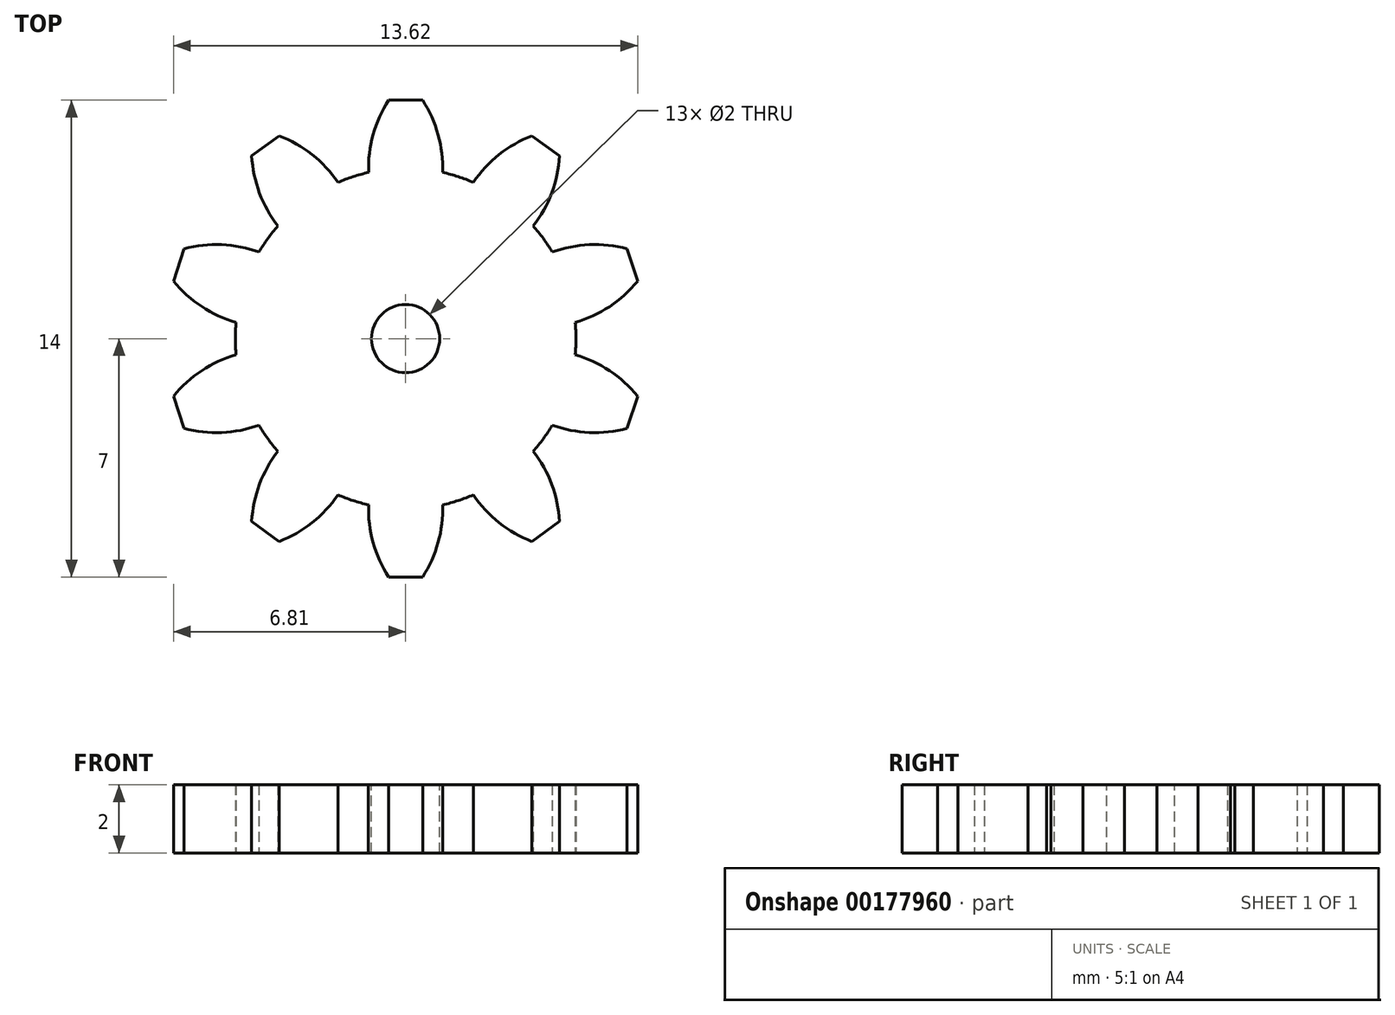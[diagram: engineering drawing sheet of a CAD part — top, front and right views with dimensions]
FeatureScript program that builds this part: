
annotation { "Feature Type Name" : "Feature", "Feature Type Description" : "" }
export const myFeature = defineFeature(function(context is Context, id is Id, definition is map)
    precondition{}
    {
        {
            var Q0;
            Q0=qCreatedBy(makeId("Top.planeOp"),FACE);
            var sketch = newSketch(context, id + "F0", { "sketchPlane" : qUnion([Q0])});
            skCircle(sketch, "E0", {"center": v(0, 0) * mm, "radius": 5 * mm});
            skLineSegment(sketch, "E1", {"start": v(0, 0) * mm, "end": v(0, 5) * mm, "construction": true});
            skLineSegment(sketch, "E2", {"start": v(0, 7) * mm, "end": v(-0.5, 7) * mm});
            skArc(sketch, "E3", {"start": v(-0.5, 7) * mm, "mid": v(-0.96, 5.98) * mm, "end": v(-1.09, 4.88) * mm});
            skArc(sketch, "E4.MirrorCS", {"start": v(0.5, 7) * mm, "mid": v(0.96, 5.98) * mm, "end": v(1.09, 4.88) * mm});
            skLineSegment(sketch, "E5.MirrorCS", {"start": v(0, 7) * mm, "end": v(0.5, 7) * mm});
            skArc(sketch, "E6.1.0", {"start": v(-4.52, 5.37) * mm, "mid": v(-4.3, 4.28) * mm, "end": v(-3.75, 3.3) * mm});
            skLineSegment(sketch, "E6.1.1", {"start": v(-4.11, 5.66) * mm, "end": v(-4.52, 5.37) * mm});
            skLineSegment(sketch, "E6.1.2", {"start": v(-4.11, 5.66) * mm, "end": v(-3.7, 5.96) * mm});
            skArc(sketch, "E6.1.3", {"start": v(-3.7, 5.96) * mm, "mid": v(-2.75, 5.4) * mm, "end": v(-1.99, 4.59) * mm});
            skArc(sketch, "E6.2.0", {"start": v(-6.81, 1.69) * mm, "mid": v(-5.99, 0.94) * mm, "end": v(-4.98, 0.47) * mm});
            skLineSegment(sketch, "E6.2.1", {"start": v(-6.66, 2.16) * mm, "end": v(-6.81, 1.69) * mm});
            skLineSegment(sketch, "E6.2.2", {"start": v(-6.66, 2.16) * mm, "end": v(-6.5, 2.64) * mm});
            skArc(sketch, "E6.2.3", {"start": v(-6.5, 2.64) * mm, "mid": v(-5.4, 2.76) * mm, "end": v(-4.3, 2.54) * mm});
            skArc(sketch, "E6.3.0", {"start": v(-6.5, -2.64) * mm, "mid": v(-5.4, -2.76) * mm, "end": v(-4.3, -2.54) * mm});
            skLineSegment(sketch, "E6.3.1", {"start": v(-6.66, -2.16) * mm, "end": v(-6.5, -2.64) * mm});
            skLineSegment(sketch, "E6.3.2", {"start": v(-6.66, -2.16) * mm, "end": v(-6.81, -1.69) * mm});
            skArc(sketch, "E6.3.3", {"start": v(-6.81, -1.69) * mm, "mid": v(-5.99, -0.94) * mm, "end": v(-4.98, -0.47) * mm});
            skArc(sketch, "E6.4.0", {"start": v(-3.7, -5.96) * mm, "mid": v(-2.75, -5.4) * mm, "end": v(-1.99, -4.59) * mm});
            skLineSegment(sketch, "E6.4.1", {"start": v(-4.11, -5.66) * mm, "end": v(-3.7, -5.96) * mm});
            skLineSegment(sketch, "E6.4.2", {"start": v(-4.11, -5.66) * mm, "end": v(-4.52, -5.37) * mm});
            skArc(sketch, "E6.4.3", {"start": v(-4.52, -5.37) * mm, "mid": v(-4.3, -4.28) * mm, "end": v(-3.75, -3.3) * mm});
            skArc(sketch, "E6.5.0", {"start": v(0.5, -7) * mm, "mid": v(0.96, -5.98) * mm, "end": v(1.09, -4.88) * mm});
            skLineSegment(sketch, "E6.5.1", {"start": v(0, -7) * mm, "end": v(0.5, -7) * mm});
            skLineSegment(sketch, "E6.5.2", {"start": v(0, -7) * mm, "end": v(-0.5, -7) * mm});
            skArc(sketch, "E6.5.3", {"start": v(-0.5, -7) * mm, "mid": v(-0.96, -5.98) * mm, "end": v(-1.09, -4.88) * mm});
            skArc(sketch, "E6.6.0", {"start": v(4.52, -5.37) * mm, "mid": v(4.3, -4.28) * mm, "end": v(3.75, -3.3) * mm});
            skLineSegment(sketch, "E6.6.1", {"start": v(4.11, -5.66) * mm, "end": v(4.52, -5.37) * mm});
            skLineSegment(sketch, "E6.6.2", {"start": v(4.11, -5.66) * mm, "end": v(3.7, -5.96) * mm});
            skArc(sketch, "E6.6.3", {"start": v(3.7, -5.96) * mm, "mid": v(2.75, -5.4) * mm, "end": v(1.99, -4.59) * mm});
            skArc(sketch, "E6.7.0", {"start": v(6.81, -1.69) * mm, "mid": v(5.99, -0.94) * mm, "end": v(4.98, -0.47) * mm});
            skLineSegment(sketch, "E6.7.1", {"start": v(6.66, -2.16) * mm, "end": v(6.81, -1.69) * mm});
            skLineSegment(sketch, "E6.7.2", {"start": v(6.66, -2.16) * mm, "end": v(6.5, -2.64) * mm});
            skArc(sketch, "E6.7.3", {"start": v(6.5, -2.64) * mm, "mid": v(5.4, -2.76) * mm, "end": v(4.3, -2.54) * mm});
            skArc(sketch, "E6.8.0", {"start": v(6.5, 2.64) * mm, "mid": v(5.4, 2.76) * mm, "end": v(4.3, 2.54) * mm});
            skLineSegment(sketch, "E6.8.1", {"start": v(6.66, 2.16) * mm, "end": v(6.5, 2.64) * mm});
            skLineSegment(sketch, "E6.8.2", {"start": v(6.66, 2.16) * mm, "end": v(6.81, 1.69) * mm});
            skArc(sketch, "E6.8.3", {"start": v(6.81, 1.69) * mm, "mid": v(5.99, 0.94) * mm, "end": v(4.98, 0.47) * mm});
            skArc(sketch, "E6.9.0", {"start": v(3.7, 5.96) * mm, "mid": v(2.75, 5.4) * mm, "end": v(1.99, 4.59) * mm});
            skLineSegment(sketch, "E6.9.1", {"start": v(4.11, 5.66) * mm, "end": v(3.7, 5.96) * mm});
            skLineSegment(sketch, "E6.9.2", {"start": v(4.11, 5.66) * mm, "end": v(4.52, 5.37) * mm});
            skArc(sketch, "E6.9.3", {"start": v(4.52, 5.37) * mm, "mid": v(4.3, 4.28) * mm, "end": v(3.75, 3.3) * mm});
            skSolve(sketch);
        }
        {
            var Q0;
            Q0=qSketchRegion(id+"F0",true);
            extrude(context, id + "F1", {"entities" : qUnion([Q0]), "depth" : 2 * mm});
        }
        {
            var Q0;
            Q0=makeQuery(id+"F1.opExtrude","CAP_FACE",FACE,{"disambiguationData":[OSD([sQuery(id+"F0.wireOp",EDGE,"E0"),sQuery(id+"F0.wireOp",EDGE,"E2"),sQuery(id+"F0.wireOp",EDGE,"E3"),sQuery(id+"F0.wireOp",EDGE,"E4.MirrorCS"),sQuery(id+"F0.wireOp",EDGE,"E5.MirrorCS"),sQuery(id+"F0.wireOp",EDGE,"E6.1.0"),sQuery(id+"F0.wireOp",EDGE,"E6.1.1"),sQuery(id+"F0.wireOp",EDGE,"E6.1.2"),sQuery(id+"F0.wireOp",EDGE,"E6.1.3"),sQuery(id+"F0.wireOp",EDGE,"E6.2.0"),sQuery(id+"F0.wireOp",EDGE,"E6.2.1"),sQuery(id+"F0.wireOp",EDGE,"E6.2.2"),sQuery(id+"F0.wireOp",EDGE,"E6.2.3"),sQuery(id+"F0.wireOp",EDGE,"E6.3.0"),sQuery(id+"F0.wireOp",EDGE,"E6.3.1"),sQuery(id+"F0.wireOp",EDGE,"E6.3.2"),sQuery(id+"F0.wireOp",EDGE,"E6.3.3"),sQuery(id+"F0.wireOp",EDGE,"E6.4.0"),sQuery(id+"F0.wireOp",EDGE,"E6.4.1"),sQuery(id+"F0.wireOp",EDGE,"E6.4.2"),sQuery(id+"F0.wireOp",EDGE,"E6.4.3"),sQuery(id+"F0.wireOp",EDGE,"E6.5.0"),sQuery(id+"F0.wireOp",EDGE,"E6.5.1"),sQuery(id+"F0.wireOp",EDGE,"E6.5.2"),sQuery(id+"F0.wireOp",EDGE,"E6.5.3"),sQuery(id+"F0.wireOp",EDGE,"E6.6.0"),sQuery(id+"F0.wireOp",EDGE,"E6.6.1"),sQuery(id+"F0.wireOp",EDGE,"E6.6.2"),sQuery(id+"F0.wireOp",EDGE,"E6.6.3"),sQuery(id+"F0.wireOp",EDGE,"E6.7.0"),sQuery(id+"F0.wireOp",EDGE,"E6.7.1"),sQuery(id+"F0.wireOp",EDGE,"E6.7.2"),sQuery(id+"F0.wireOp",EDGE,"E6.7.3"),sQuery(id+"F0.wireOp",EDGE,"E6.8.0"),sQuery(id+"F0.wireOp",EDGE,"E6.8.1"),sQuery(id+"F0.wireOp",EDGE,"E6.8.2"),sQuery(id+"F0.wireOp",EDGE,"E6.8.3"),sQuery(id+"F0.wireOp",EDGE,"E6.9.0"),sQuery(id+"F0.wireOp",EDGE,"E6.9.1"),sQuery(id+"F0.wireOp",EDGE,"E6.9.2"),sQuery(id+"F0.wireOp",EDGE,"E6.9.3"),sQuery(id+"F0.wireOp",EDGE,"E6.10.0"),sQuery(id+"F0.wireOp",EDGE,"E6.10.1"),sQuery(id+"F0.wireOp",EDGE,"E6.10.2"),sQuery(id+"F0.wireOp",EDGE,"E6.10.3"),sQuery(id+"F0.wireOp",EDGE,"E6.11.0"),sQuery(id+"F0.wireOp",EDGE,"E6.11.1"),sQuery(id+"F0.wireOp",EDGE,"E6.11.2"),sQuery(id+"F0.wireOp",EDGE,"E6.11.3"),sQuery(id+"F0.wireOp",EDGE,"E6.12.0"),sQuery(id+"F0.wireOp",EDGE,"E6.12.1"),sQuery(id+"F0.wireOp",EDGE,"E6.12.2"),sQuery(id+"F0.wireOp",EDGE,"E6.12.3"),sQuery(id+"F0.wireOp",EDGE,"E6.13.0"),sQuery(id+"F0.wireOp",EDGE,"E6.13.1"),sQuery(id+"F0.wireOp",EDGE,"E6.13.2"),sQuery(id+"F0.wireOp",EDGE,"E6.13.3"),sQuery(id+"F0.wireOp",EDGE,"E6.14.0"),sQuery(id+"F0.wireOp",EDGE,"E6.14.1"),sQuery(id+"F0.wireOp",EDGE,"E6.14.2"),sQuery(id+"F0.wireOp",EDGE,"E6.14.3"),sQuery(id+"F0.wireOp",EDGE,"E6.15.0"),sQuery(id+"F0.wireOp",EDGE,"E6.15.1"),sQuery(id+"F0.wireOp",EDGE,"E6.15.2"),sQuery(id+"F0.wireOp",EDGE,"E6.15.3")])],"isStart":false});
            var sketch = newSketch(context, id + "F2", { "sketchPlane" : qUnion([Q0])});
            skCircle(sketch, "E7", {"center": v(0, 0) * mm, "radius": 1 * mm});
            skSolve(sketch);
        }
        {
            var Q0;
            Q0=qSketchRegion(id+"F2",true);
            extrude(context, id + "F3", {"entities" : qUnion([Q0]), "operationType" : NewBodyOperationType.REMOVE, "endBound" : BoundingType.THROUGH_ALL, "oppositeDirection" : true, "depth" : 25 * mm});
        }
    });
